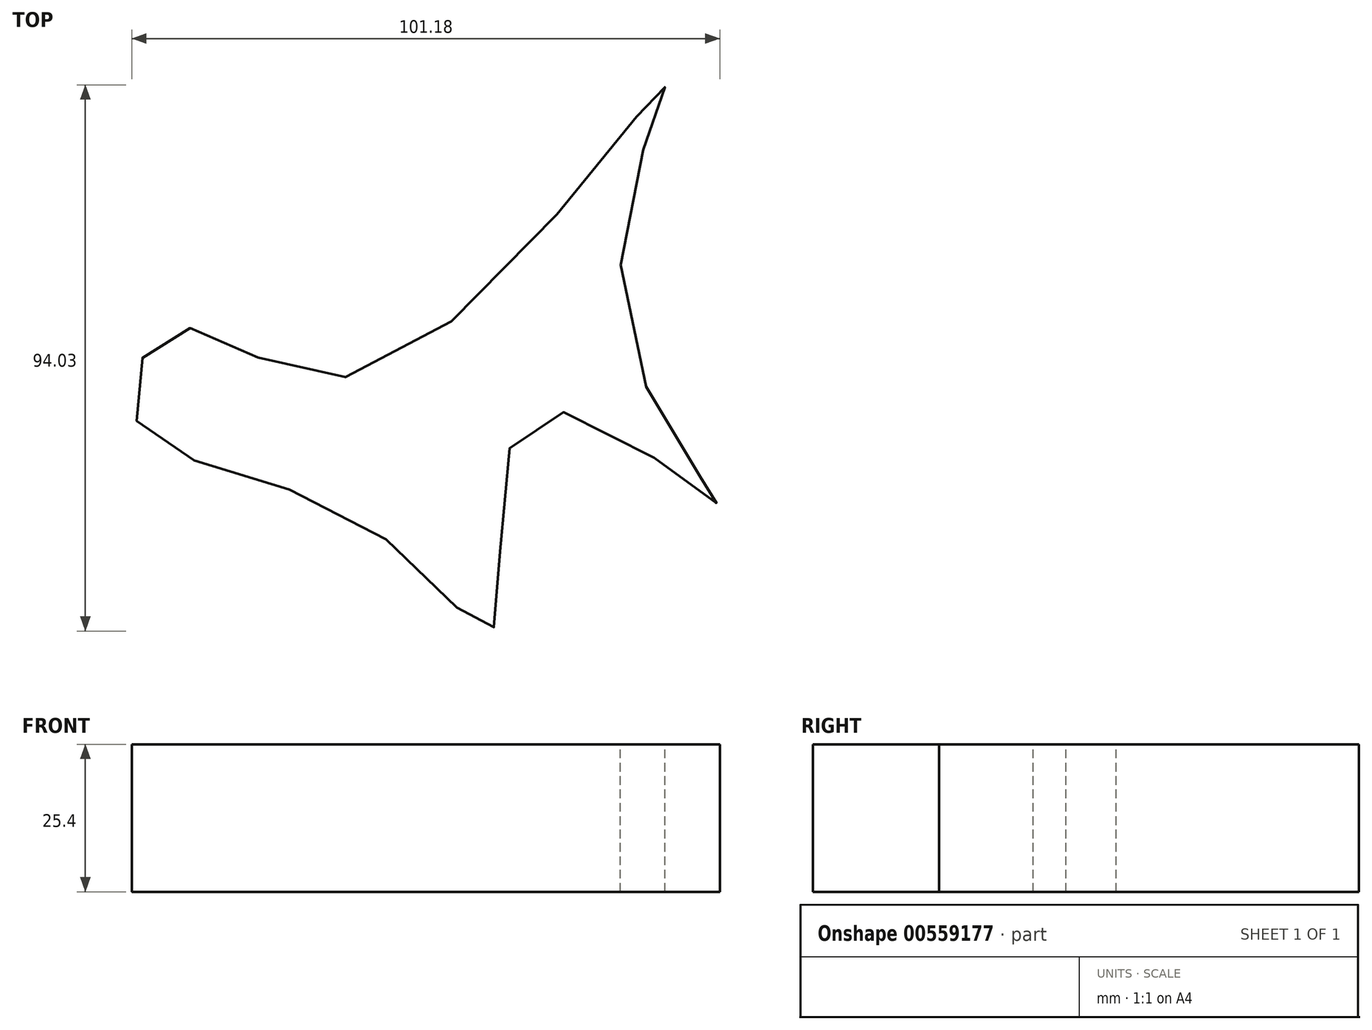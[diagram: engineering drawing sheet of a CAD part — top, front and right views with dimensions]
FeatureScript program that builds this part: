
annotation { "Feature Type Name" : "Feature", "Feature Type Description" : "" }
export const myFeature = defineFeature(function(context is Context, id is Id, definition is map)
    precondition{}
    {
        {
            var Q0;
            Q0=qCreatedBy(makeId("Top.planeOp"),FACE);
            var sketch = newSketch(context, id + "F0", { "sketchPlane" : qUnion([Q0])});
            skFitSpline(sketch, "E0", {"points": [v(-209.73, -100.33) * mm, v(-203.05, -84.46) * mm, v(-171.21, -92.3) * mm, v(-119.1, -42.54) * mm, v(-126.08, -81.53) * mm, v(-109.68, -114.67) * mm, v(-141.55, -99.2) * mm, v(-148.25, -135.85) * mm, v(-170.51, -118.1) * mm, v(-209.73, -100.33) * mm]});
            skSolve(sketch);
        }
        {
            var Q0;
            Q0=sQuery(id+"F0.wireOp",EDGE,"E0");
            extrude(context, id + "F1", {"bodyType" : ToolBodyType.SURFACE, "surfaceEntities" : qUnion([Q0]), "depth" : 25.4 * mm, "offsetDistance" : 25.4 * mm});
        }
    });
